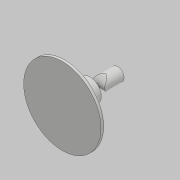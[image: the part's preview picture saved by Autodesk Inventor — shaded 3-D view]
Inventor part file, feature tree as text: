
AUTODESK INVENTOR PART (.ipt)
format: ipt  version: 2018 (Build 220112000, 112)  size: 218,112 bytes
history: native  units: mm
features: other x13, sketch x13, extrude x4, projected_geometry x2, fillet x1, plane x1, loft x1, mirror x1
ambient origin geometry x8: Origin, YZ Plane, XZ Plane, XY Plane, X Axis, Y Axis, Z Axis, Center Point
bodies: Body1 (feature_tree), Body2 (feature_tree), Body3 (feature_tree), Body4 (feature_tree), Body5 (feature_tree)
feature tree (36):
  other  "實體1"
  other  "迴轉1"
  other  "迴轉2"
  fillet  "圓角1"  Radius=6.0mm
  sketch  "草圖3"
  other  "迴轉3"
  sketch  "3D 草圖1"
  plane  "工作平面1"
  other  "迴轉4"
  extrude  "擠出1"  Depth=60.0mm
  extrude  "擠出2"  TaperAngle=90.0deg  [1 undecoded]
  other  "刪除面1"
  other  "刪除面2"
  other  "迴轉5"
  other  "迴轉6"
  sketch  "草圖16"
  extrude  "擠出3"  Depth=40.0mm
  extrude  "擠出4"  Depth=17.5mm
  other  "直接編輯1"
  loft  "斷面混成2"
  mirror  "鏡射1"
  sketch  "草圖1"
  sketch  "草圖2"
  sketch  "草圖8"
  sketch  "草圖9"
  sketch  "草圖10"
  sketch  "草圖11"
  sketch  "草圖12"
  projected_geometry  "投影迴路1"
  sketch  "草圖13"
  sketch  "草圖14"
  sketch  "草圖15"
  other  "Srf2"
  projected_geometry  "投影迴路2"
  other  "擠出表面1"
  other  "移動1"
note: 1 required parameter value undecoded (feature->parameter linkage not recoverable at this tier; creation-order binding heuristic only, values carry confidence <= 0.55)
